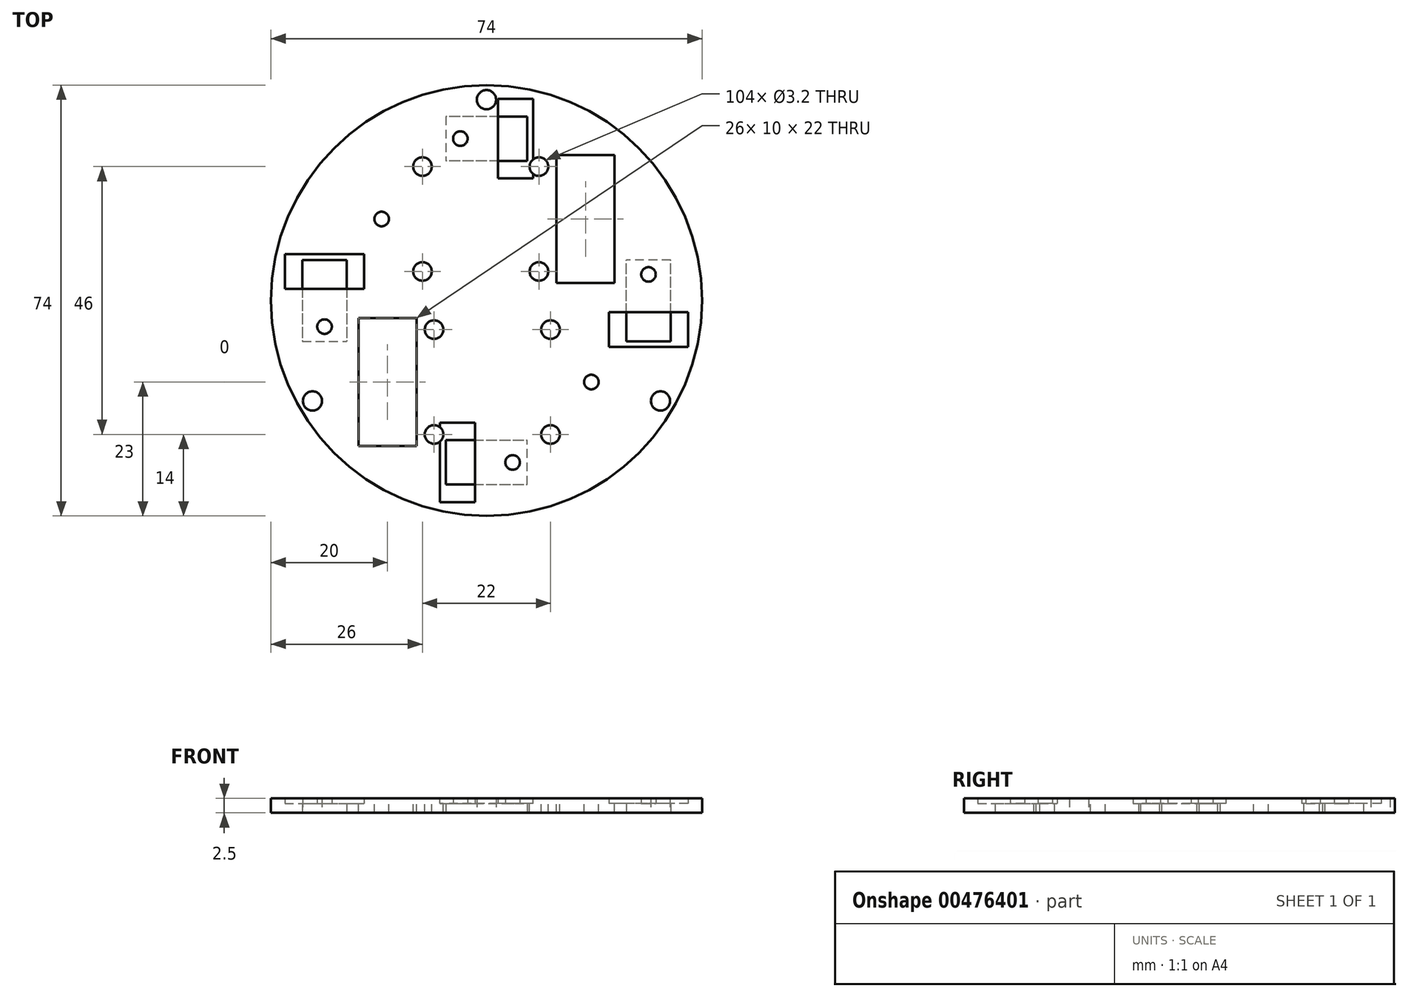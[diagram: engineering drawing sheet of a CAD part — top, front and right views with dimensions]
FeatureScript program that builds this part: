
annotation { "Feature Type Name" : "Feature", "Feature Type Description" : "" }
export const myFeature = defineFeature(function(context is Context, id is Id, definition is map)
    precondition{}
    {
        {
            var Q0;
            Q0=qCreatedBy(makeId("Top.planeOp"),FACE);
            var sketch = newSketch(context, id + "F0", { "sketchPlane" : qUnion([Q0])});
            skCircle(sketch, "E0", {"center": v(0, 0) * mm, "radius": 37 * mm});
            skCircle(sketch, "E1", {"center": v(0, 34.5) * mm, "radius": 1.65 * mm});
            skLineSegment(sketch, "E2", {"start": v(0, 0) * mm, "end": v(0, 34.5) * mm});
            skCircle(sketch, "E3.1.0", {"center": v(-29.88, -17.25) * mm, "radius": 1.65 * mm});
            skCircle(sketch, "E3.2.0", {"center": v(29.88, -17.25) * mm, "radius": 1.65 * mm});
            skSolve(sketch);
        }
        {
            var Q0;
            Q0=qSketchRegion(id+"F0",true);
            extrude(context, id + "F1", {"entities" : qUnion([Q0]), "depth" : 2.5 * mm});
        }
        {
            var Q0;
            Q0=makeQuery(id+"F1.opExtrude","CAP_FACE",FACE,{"disambiguationData":[OSD([sQuery(id+"F0.wireOp",EDGE,"E0"),sQuery(id+"F0.wireOp",EDGE,"E1"),sQuery(id+"F0.wireOp",EDGE,"E3.1.0"),sQuery(id+"F0.wireOp",EDGE,"E3.2.0")])],"isStart":false});
            var sketch = newSketch(context, id + "F2", { "sketchPlane" : qUnion([Q0])});
            skLineSegment(sketch, "E4.top", {"start": v(-22, -25) * mm, "end": v(-12, -25) * mm});
            skLineSegment(sketch, "E4.right", {"start": v(-22, -3) * mm, "end": v(-22, -25) * mm});
            skLineSegment(sketch, "E5.bottom", {"start": v(-12, -20) * mm, "end": v(14, -20) * mm, "construction": true});
            skLineSegment(sketch, "E5.top", {"start": v(-22, -8) * mm, "end": v(14, -8) * mm, "construction": true});
            skLineSegment(sketch, "E5.right", {"start": v(14, -20) * mm, "end": v(14, -8) * mm, "construction": true});
            skLineSegment(sketch, "E6", {"start": v(-22, -8) * mm, "end": v(-22, -7) * mm, "construction": true});
            skLineSegment(sketch, "E7", {"start": v(-22, -7) * mm, "end": v(14, -7) * mm, "construction": true});
            skLineSegment(sketch, "E8", {"start": v(14, -7) * mm, "end": v(14, -8) * mm, "construction": true});
            skLineSegment(sketch, "E9", {"start": v(-4, -7) * mm, "end": v(-4, 0) * mm, "construction": true});
            skLineSegment(sketch, "E10", {"start": v(-4, 0) * mm, "end": v(0, 0) * mm, "construction": true});
            skLineSegment(sketch, "E11", {"start": v(14, -14) * mm, "end": v(18, -14) * mm});
            skCircle(sketch, "E12", {"center": v(18, -14) * mm, "radius": 1.25 * mm});
            skCircle(sketch, "E13", {"center": v(-9, -23) * mm, "radius": 1.6 * mm});
            skCircle(sketch, "E14", {"center": v(11, -23) * mm, "radius": 1.6 * mm});
            skLineSegment(sketch, "E15", {"start": v(-9, -23) * mm, "end": v(11, -23) * mm, "construction": true});
            skLineSegment(sketch, "E16", {"start": v(1, -23) * mm, "end": v(1, -20) * mm, "construction": true});
            skLineSegment(sketch, "E17", {"start": v(-12, -14) * mm, "end": v(14, -14) * mm, "construction": true});
            skCircle(sketch, "E18.0.MirrorC", {"center": v(11, -5) * mm, "radius": 1.6 * mm});
            skCircle(sketch, "E18.1.MirrorC", {"center": v(-9, -5) * mm, "radius": 1.6 * mm});
            skPoint(sketch, "E19.center", {"position": v(0, 0) * mm});
            skLineSegment(sketch, "E20", {"start": v(-22, -3) * mm, "end": v(-12, -3) * mm});
            skLineSegment(sketch, "E21", {"start": v(-12, -25) * mm, "end": v(-12, -20) * mm});
            skLineSegment(sketch, "E22", {"start": v(-12, -20) * mm, "end": v(-12, -14) * mm});
            skLineSegment(sketch, "E23", {"start": v(-12, -14) * mm, "end": v(-12, -8) * mm});
            skLineSegment(sketch, "E24", {"start": v(-12, -8) * mm, "end": v(-12, -3) * mm});
            skLineSegment(sketch, "E25.1.0", {"start": v(22, 3) * mm, "end": v(12, 3) * mm});
            skLineSegment(sketch, "E25.1.1", {"start": v(22, 3) * mm, "end": v(22, 25) * mm});
            skLineSegment(sketch, "E25.1.2", {"start": v(22, 25) * mm, "end": v(12, 25) * mm});
            skLineSegment(sketch, "E25.1.3", {"start": v(12, 25) * mm, "end": v(12, 20) * mm});
            skLineSegment(sketch, "E25.1.4", {"start": v(12, 20) * mm, "end": v(12, 14) * mm});
            skLineSegment(sketch, "E25.1.5", {"start": v(12, 14) * mm, "end": v(12, 8) * mm});
            skLineSegment(sketch, "E25.1.6", {"start": v(12, 8) * mm, "end": v(12, 3) * mm});
            skCircle(sketch, "E25.1.7", {"center": v(9, 5) * mm, "radius": 1.6 * mm});
            skCircle(sketch, "E25.1.8", {"center": v(-11, 5) * mm, "radius": 1.6 * mm});
            skCircle(sketch, "E25.1.9", {"center": v(-18, 14) * mm, "radius": 1.25 * mm});
            skCircle(sketch, "E25.1.10", {"center": v(-11, 23) * mm, "radius": 1.6 * mm});
            skCircle(sketch, "E25.1.11", {"center": v(9, 23) * mm, "radius": 1.6 * mm});
            skSolve(sketch);
        }
        {
            var Q0;
            Q0=qSketchRegion(id+"F2",true);
            extrude(context, id + "F3", {"entities" : qUnion([Q0]), "operationType" : NewBodyOperationType.REMOVE, "endBound" : BoundingType.UP_TO_NEXT, "oppositeDirection" : true, "depth" : 25 * mm});
        }
        {
            var Q0;
            Q0=makeQuery(id+"F1.opExtrude","CAP_FACE",FACE,{"disambiguationData":[OSD([sQuery(id+"F0.wireOp",EDGE,"E0"),sQuery(id+"F0.wireOp",EDGE,"E1"),sQuery(id+"F0.wireOp",EDGE,"E3.1.0"),sQuery(id+"F0.wireOp",EDGE,"E3.2.0")])],"isStart":true});
            var sketch = newSketch(context, id + "F4", { "sketchPlane" : qUnion([Q0])});
            skLineSegment(sketch, "E26.bottom", {"start": v(-6.99, 31.62) * mm, "end": v(6.98, 31.62) * mm});
            skLineSegment(sketch, "E26.top", {"start": v(-6.98, 24) * mm, "end": v(6.98, 24) * mm});
            skLineSegment(sketch, "E26.left", {"start": v(-6.99, 31.62) * mm, "end": v(-6.99, 24) * mm});
            skLineSegment(sketch, "E26.right", {"start": v(6.98, 31.62) * mm, "end": v(6.98, 24) * mm});
            skLineSegment(sketch, "E27", {"start": v(0, 0) * mm, "end": v(0, 24) * mm, "construction": true});
            skLineSegment(sketch, "E28.1.0", {"start": v(-31.62, -6.98) * mm, "end": v(-31.62, 6.98) * mm});
            skLineSegment(sketch, "E28.1.1", {"start": v(-31.62, -6.99) * mm, "end": v(-24, -6.99) * mm});
            skLineSegment(sketch, "E28.1.2", {"start": v(-24, -6.98) * mm, "end": v(-24, 6.98) * mm});
            skLineSegment(sketch, "E28.1.3", {"start": v(-31.62, 6.98) * mm, "end": v(-24, 6.98) * mm});
            skLineSegment(sketch, "E28.2.0", {"start": v(6.98, -31.62) * mm, "end": v(-6.99, -31.62) * mm});
            skLineSegment(sketch, "E28.2.1", {"start": v(6.99, -31.62) * mm, "end": v(6.99, -24) * mm});
            skLineSegment(sketch, "E28.2.2", {"start": v(6.98, -24) * mm, "end": v(-6.98, -24) * mm});
            skLineSegment(sketch, "E28.2.3", {"start": v(-6.98, -31.62) * mm, "end": v(-6.98, -24) * mm});
            skLineSegment(sketch, "E28.3.0", {"start": v(31.62, 6.99) * mm, "end": v(31.62, -6.98) * mm});
            skLineSegment(sketch, "E28.3.1", {"start": v(31.62, 6.99) * mm, "end": v(24, 6.99) * mm});
            skLineSegment(sketch, "E28.3.2", {"start": v(24, 6.98) * mm, "end": v(24, -6.98) * mm});
            skLineSegment(sketch, "E28.3.3", {"start": v(31.62, -6.98) * mm, "end": v(24, -6.98) * mm});
            skPoint(sketch, "E28.center", {"position": v(0, 0) * mm});
            skSolve(sketch);
        }
        {
            var Q0;
            Q0=qSketchRegion(id+"F4",true);
            extrude(context, id + "F5", {"entities" : qUnion([Q0]), "operationType" : NewBodyOperationType.REMOVE, "oppositeDirection" : true, "depth" : 1.6 * mm});
        }
        {
            var Q0;
            Q0=makeQuery(id+"F5.boolean.opBoolean","COPY",FACE,{"derivedFrom":makeQuery(id+"F5.opExtrude","CAP_FACE",FACE,{"disambiguationData":[OSD([sQuery(id+"F4.wireOp",EDGE,"E26.bottom"),sQuery(id+"F4.wireOp",EDGE,"E26.top"),sQuery(id+"F4.wireOp",EDGE,"E26.left"),sQuery(id+"F4.wireOp",EDGE,"E26.right")])],"isStart":false})});
            var sketch = newSketch(context, id + "F6", { "sketchPlane" : qUnion([Q0])});
            skLineSegment(sketch, "E29", {"start": v(6.98, 27.81) * mm, "end": v(4.48, 27.81) * mm});
            skLineSegment(sketch, "E30.bottom", {"start": v(-7.99, 34.62) * mm, "end": v(-1.99, 34.62) * mm});
            skLineSegment(sketch, "E30.top", {"start": v(-7.99, 21) * mm, "end": v(-1.99, 21) * mm});
            skLineSegment(sketch, "E30.left", {"start": v(-7.99, 34.62) * mm, "end": v(-7.99, 21) * mm});
            skLineSegment(sketch, "E30.right", {"start": v(-1.99, 34.62) * mm, "end": v(-1.99, 21) * mm});
            skCircle(sketch, "E31", {"center": v(4.48, 27.81) * mm, "radius": 1.25 * mm});
            skLineSegment(sketch, "E32.1.0", {"start": v(-34.62, -7.99) * mm, "end": v(-34.62, -1.99) * mm});
            skLineSegment(sketch, "E32.1.1", {"start": v(-34.62, -7.99) * mm, "end": v(-21, -7.98) * mm});
            skLineSegment(sketch, "E32.1.2", {"start": v(-21, -7.99) * mm, "end": v(-21, -1.99) * mm});
            skLineSegment(sketch, "E32.1.3", {"start": v(-34.62, -1.99) * mm, "end": v(-21, -1.98) * mm});
            skCircle(sketch, "E32.1.4", {"center": v(-27.81, 4.48) * mm, "radius": 1.25 * mm});
            skLineSegment(sketch, "E32.2.0", {"start": v(7.98, -34.62) * mm, "end": v(1.98, -34.62) * mm});
            skLineSegment(sketch, "E32.2.1", {"start": v(7.99, -34.62) * mm, "end": v(7.98, -21) * mm});
            skLineSegment(sketch, "E32.2.2", {"start": v(7.99, -21) * mm, "end": v(1.98, -21) * mm});
            skLineSegment(sketch, "E32.2.3", {"start": v(1.99, -34.62) * mm, "end": v(1.98, -21) * mm});
            skCircle(sketch, "E32.2.4", {"center": v(-4.48, -27.81) * mm, "radius": 1.25 * mm});
            skLineSegment(sketch, "E32.3.0", {"start": v(34.62, 7.99) * mm, "end": v(34.62, 1.99) * mm});
            skLineSegment(sketch, "E32.3.1", {"start": v(34.62, 7.99) * mm, "end": v(21, 7.99) * mm});
            skLineSegment(sketch, "E32.3.2", {"start": v(21, 7.99) * mm, "end": v(21, 1.99) * mm});
            skLineSegment(sketch, "E32.3.3", {"start": v(34.62, 1.99) * mm, "end": v(21, 1.99) * mm});
            skCircle(sketch, "E32.3.4", {"center": v(27.81, -4.48) * mm, "radius": 1.25 * mm});
            skPoint(sketch, "E32.center", {"position": v(0, 0) * mm});
            skSolve(sketch);
        }
        {
            var Q0;
            Q0=qSketchRegion(id+"F6",true);
            extrude(context, id + "F7", {"entities" : qUnion([Q0]), "operationType" : NewBodyOperationType.REMOVE, "endBound" : BoundingType.UP_TO_NEXT, "oppositeDirection" : true, "depth" : 25 * mm});
        }
    });
